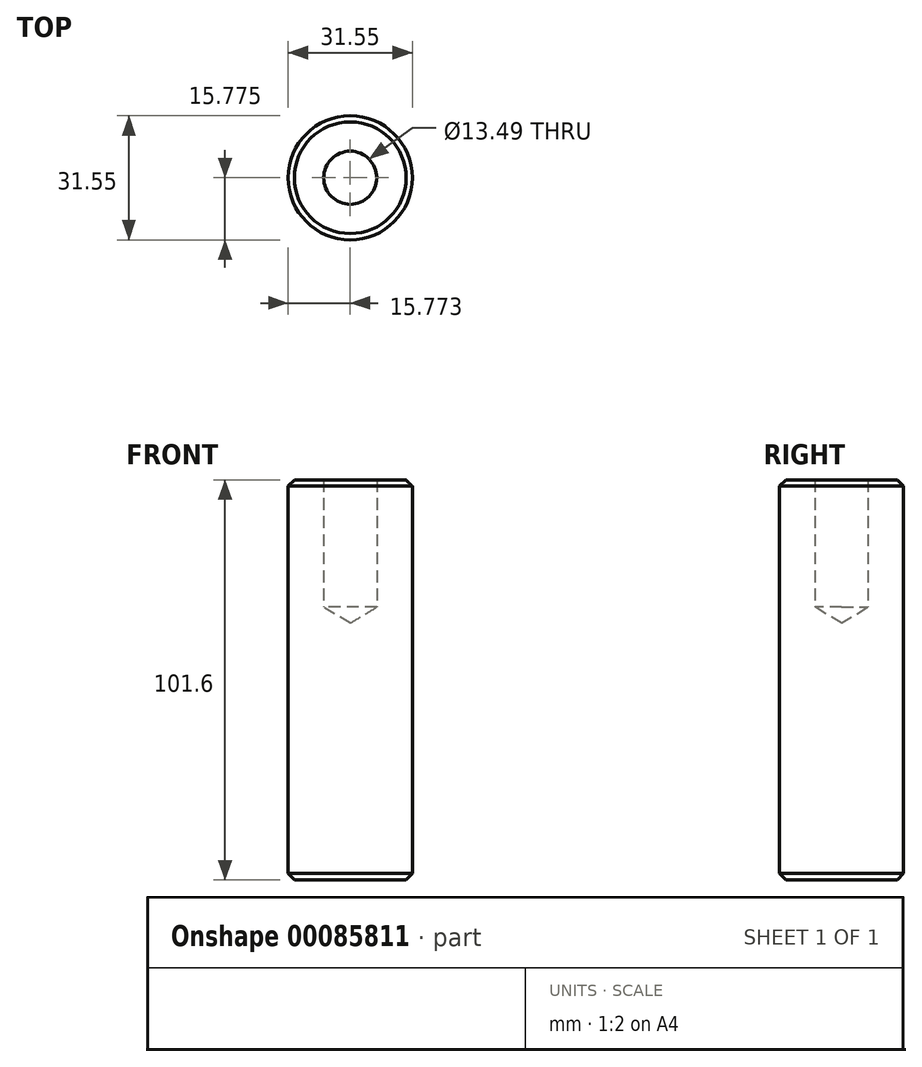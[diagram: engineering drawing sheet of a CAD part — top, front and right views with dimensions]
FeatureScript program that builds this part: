
annotation { "Feature Type Name" : "Feature", "Feature Type Description" : "" }
export const myFeature = defineFeature(function(context is Context, id is Id, definition is map)
    precondition{}
    {
        {
            var Q0;
            Q0=qCreatedBy(makeId("Top.planeOp"),FACE);
            var sketch = newSketch(context, id + "F0", { "sketchPlane" : qUnion([Q0])});
            skCircle(sketch, "E0", {"center": v(-36.88, 14.12) * mm, "radius": 15.77 * mm});
            skSolve(sketch);
        }
        {
            var Q0;
            Q0=makeQuery(id+"F0.imprint","IMPRINT",FACE,{"disambiguationData":[TD([[makeQuery(id+"F0.imprint","IMPRINT",EDGE,{"derivedFrom":sQuery(id+"F0.wireOp",EDGE,"E0")}),1.0]])]});
            extrude(context, id + "F1", {"entities" : qUnion([Q0]), "depth" : 101.6 * mm, "offsetDistance" : 25.4 * mm});
        }
        {
            var Q0;
            Q0=makeQuery(id+"F1.opExtrude","CAP_FACE",FACE,{"disambiguationData":[OSD([sQuery(id+"F0.wireOp",EDGE,"E0")])],"isStart":false});
            var sketch = newSketch(context, id + "F2", { "sketchPlane" : qUnion([Q0])});
            skPoint(sketch, "E1", {"position": v(-36.88, 14.12) * mm});
            skSolve(sketch);
        }
        {
            var Q0;
            Q0=sQuery(id+"F2.wireOp",VERTEX,"E1");
            var Q1;
            Q1=makeQuery(id+"F1.opExtrude","SWEPT_BODY",BODY,{"disambiguationData":[OSD([sQuery(id+"F0.wireOp",EDGE,"E0")])]});
            hole(context, id + "F3", {"style" : HoleStyle.SIMPLE, "endStyle" : HoleEndStyle.BLIND, "standardTappedOrClearance" : lookupTablePath({ "standard" : "ANSI", "engagement" : "75%", "pitch" : "11 tpi", "size" : "5/8", "type" : "Tapped" }), "standardBlindInLast" : lookupTablePath({ "standard" : "ANSI", "fit" : "Free", "engagement" : "75%", "pitch" : "11 tpi", "size" : "5/8", "type" : "Clearance & tapped" }), "holeDiameter" : 13.5 * mm, "majorDiameter" : 15.88 * mm, "showTappedDepth" : true, "holeDepth" : 32.33 * mm, "tappedDepth" : 25.4 * mm, "tapClearance" : 3, "startFromSketch" : true, "locations" : qUnion([Q0]), "scope" : qUnion([Q1])});
        }
        {
            var Q0;
            Q0=makeQuery(id+"F1.opExtrude","CAP_EDGE",EDGE,{"disambiguationData":[OSD([sQuery(id+"F0.wireOp",EDGE,"E0")])],"isStart":true});
            var Q1;
            Q1=makeQuery(id+"F1.opExtrude","CAP_EDGE",EDGE,{"disambiguationData":[OSD([sQuery(id+"F0.wireOp",EDGE,"E0")])],"isStart":false});
            chamfer(context, id + "F4", {"entities" : qUnion([Q0, Q1]), "width" : 1.59 * mm, "tangentPropagation" : true});
        }
    });
